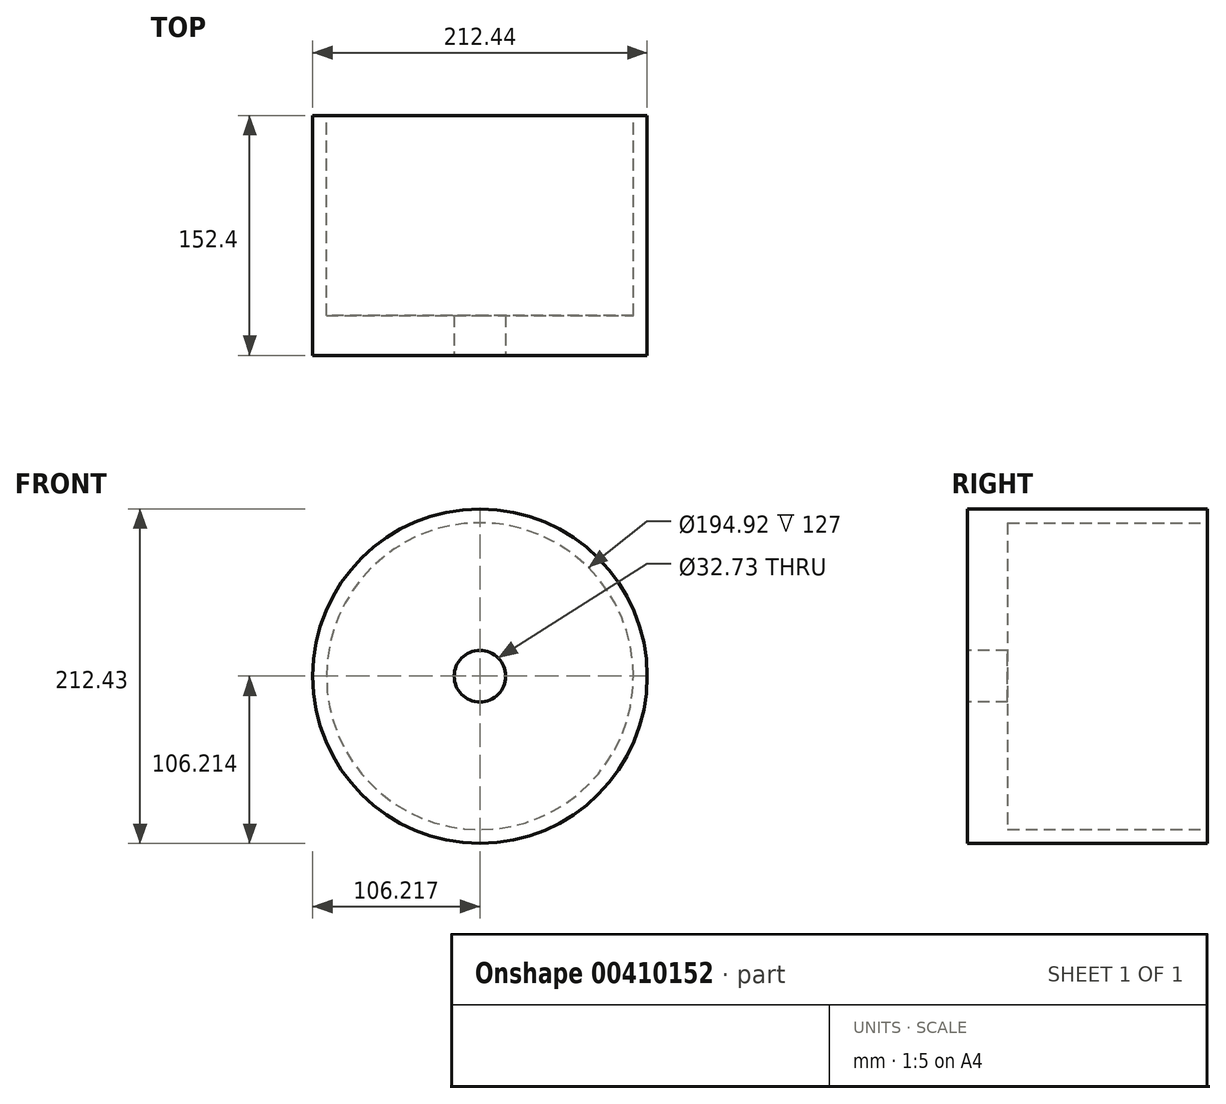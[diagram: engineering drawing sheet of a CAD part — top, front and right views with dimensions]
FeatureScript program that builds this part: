
annotation { "Feature Type Name" : "Feature", "Feature Type Description" : "" }
export const myFeature = defineFeature(function(context is Context, id is Id, definition is map)
    precondition{}
    {
        {
            var Q0;
            Q0=qCreatedBy(makeId("Front.planeOp"),FACE);
            var sketch = newSketch(context, id + "F0", { "sketchPlane" : qUnion([Q0])});
            skCircle(sketch, "E0", {"center": v(-36.33, -47.36) * mm, "radius": 106.22 * mm});
            skSolve(sketch);
        }
        {
            var Q0;
            Q0 = qSketchRegion(id + "F0", true);
            extrude(context, id + "F1", {"entities" : qUnion([Q0]), "oppositeDirection" : true, "depth" : 152.4 * mm});
        }
        {
            var Q0;
            Q0=makeQuery(id+"F1.opExtrude","CAP_FACE",FACE,{"disambiguationData":[OSD([sQuery(id+"F0.wireOp",EDGE,"E0")])],"isStart":true});
            var sketch = newSketch(context, id + "F2", { "sketchPlane" : qUnion([Q0])});
            skCircle(sketch, "E1", {"center": v(-36.33, -47.36) * mm, "radius": 101.5 * mm});
            skSolve(sketch);
        }
        {
            var Q0;
            Q0 = qSketchRegion(id + "F2", true);
            extrude(context, id + "F3", {"entities" : qUnion([Q0]), "operationType" : NewBodyOperationType.ADD, "oppositeDirection" : true, "depth" : 127 * mm});
        }
        {
            var Q0;
            Q0=makeQuery(id+"F1.opExtrude","CAP_FACE",FACE,{"disambiguationData":[OSD([sQuery(id+"F0.wireOp",EDGE,"E0")])],"isStart":false});
            var sketch = newSketch(context, id + "F4", { "sketchPlane" : qUnion([Q0])});
            skCircle(sketch, "E2", {"center": v(36.33, -47.36) * mm, "radius": 97.46 * mm});
            skSolve(sketch);
        }
        {
            var Q0;
            Q0 = qSketchRegion(id + "F4", true);
            extrude(context, id + "F5", {"entities" : qUnion([Q0]), "operationType" : NewBodyOperationType.REMOVE, "oppositeDirection" : true, "depth" : 127 * mm});
        }
        {
            var Q0;
            Q0=makeQuery(id+"F1.opExtrude","CAP_FACE",FACE,{"disambiguationData":[OSD([sQuery(id+"F0.wireOp",EDGE,"E0")])],"isStart":true});
            var sketch = newSketch(context, id + "F6", { "sketchPlane" : qUnion([Q0])});
            skCircle(sketch, "E3", {"center": v(-36.33, -47.36) * mm, "radius": 16.37 * mm});
            skSolve(sketch);
        }
        {
            var Q0;
            Q0 = qSketchRegion(id + "F6", true);
            extrude(context, id + "F7", {"entities" : qUnion([Q0]), "operationType" : NewBodyOperationType.REMOVE, "oppositeDirection" : true, "depth" : 25.4 * mm});
        }
    });
